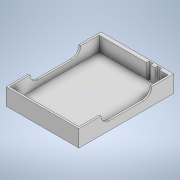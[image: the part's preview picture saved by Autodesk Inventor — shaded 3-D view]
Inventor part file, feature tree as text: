
AUTODESK INVENTOR PART (.ipt)
format: ipt  version: 2021.2 (Build 252289000, 289)  size: 210,944 bytes
history: native  units: in
note: dims shown in document units (in); Inventor stores cm internally (conversion verified against a paired STEP export)
features: sketch x8, extrude x7, fillet x1
ambient origin geometry x8: Origin, YZ Plane, XZ Plane, XY Plane, X Axis, Y Axis, Z Axis, Center Point
bodies: Solid1 (feature_tree)
feature tree (16):
  extrude  "Extrusion1"  Depth=1.8386in
  extrude  "Extrusion2"  Depth=0.7047in
  extrude  "Extrusion6"  Depth=0.0433in
  fillet  "Fillet2"  Radius=0.0433in
  sketch  "Sketch9"  dims[d8=0.0433in d9=0.0787in]
  extrude  "Extrusion9"  Depth=0.0787in
  extrude  "Extrusion10"  Depth=0.2795in
  extrude  "Extrusion11"  Depth=0.1575in
  extrude  "Extrusion12"  Depth=0.1575in
  sketch  "Sketch1"  dims[d0=1.4094in d1=1.8386in]
  sketch  "Sketch2"  dims[d2=0.9193in d3=0.7047in]
  sketch  "Sketch6"  dims[d4=0.3228in d5=0.0in d6=0.0433in d7=0.0433in]
  sketch  "Sketch10"  dims[d10=0.2795in d11=0.0in d34=0.9843in]
  sketch  "Sketch11"  dims[d35=0.4272in d36=0.1575in]
  sketch  "Sketch12"  dims[d37=0.0in d38=0.0in d39=0.1575in]
  sketch  "Sketch13"  dims[d51=0.0787in d52=0.0787in d53=0.0868in d54=0.0394in d55=0.2106in d56=0.0in d57=0.0in d58=0.0079in d59=0.0079in d60=0.0039in d61=0.0079in d62=0.2362in d63=0.0in d64=0.0in d65=0.0in d66=0.0984in d67=0.3937in d68=0.0in d20=0.0197in d21=0.0344in d22=0.0197in d23=0.0344in d25=0.0197in d26=0.0344in d27=0.0197in d28=0.0344in]
